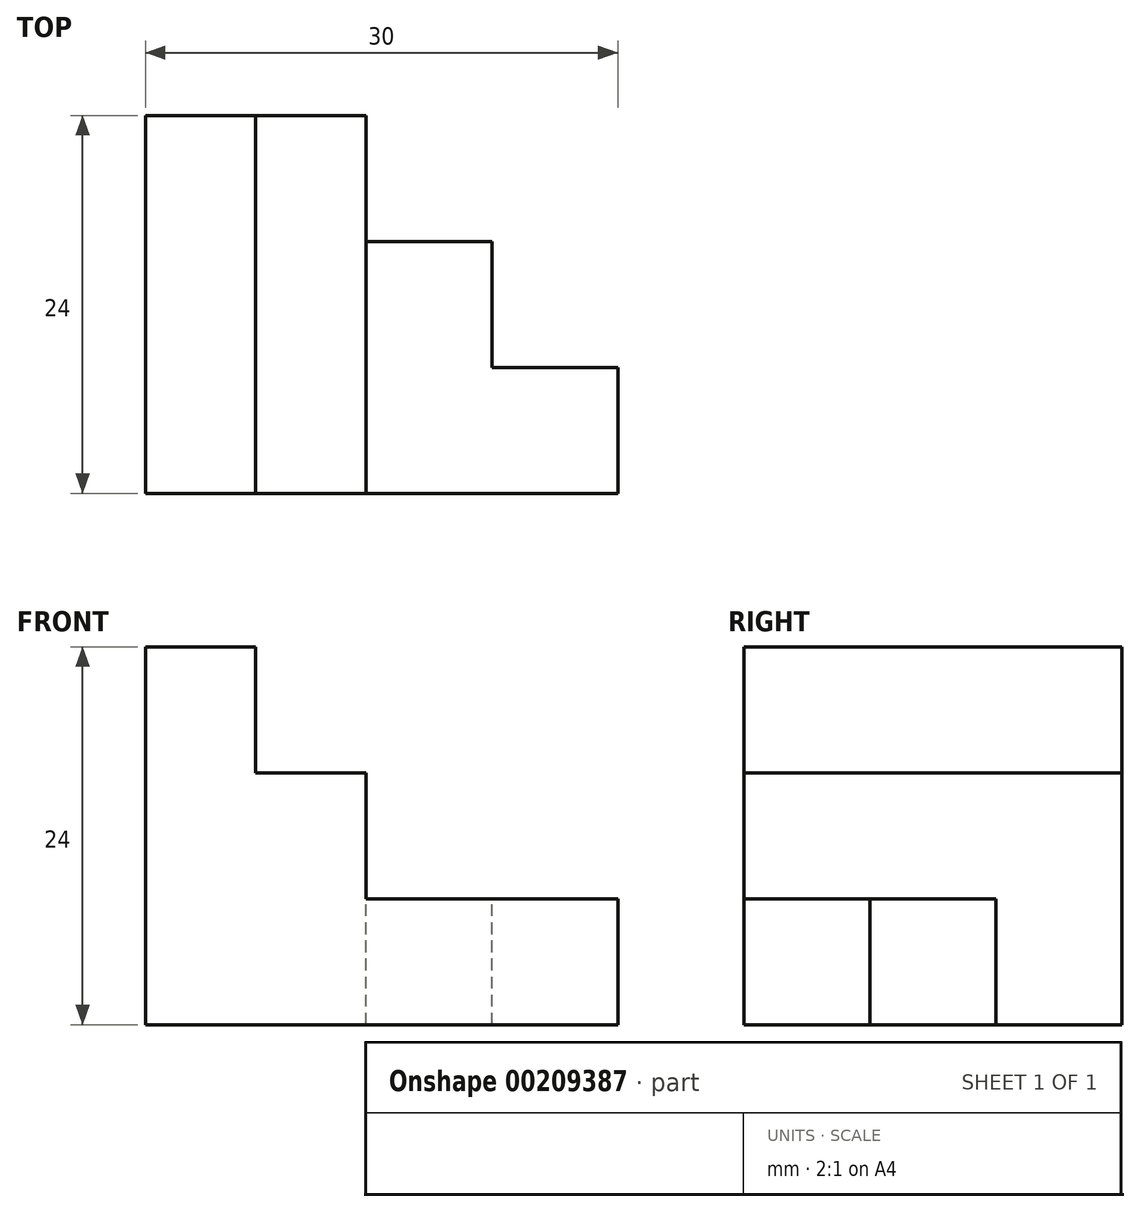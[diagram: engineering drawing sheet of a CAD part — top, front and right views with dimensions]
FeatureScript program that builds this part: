
annotation { "Feature Type Name" : "Feature", "Feature Type Description" : "" }
export const myFeature = defineFeature(function(context is Context, id is Id, definition is map)
    precondition{}
    {
        {
            var Q0;
            Q0=qCreatedBy(makeId("Top.planeOp"),FACE);
            var sketch = newSketch(context, id + "F0", { "sketchPlane" : qUnion([Q0])});
            skLineSegment(sketch, "E0.bottom", {"start": v(0, 0) * mm, "end": v(30, 0) * mm});
            skLineSegment(sketch, "E0.top", {"start": v(0, 24) * mm, "end": v(30, 24) * mm});
            skLineSegment(sketch, "E0.left", {"start": v(0, 0) * mm, "end": v(0, 24) * mm});
            skLineSegment(sketch, "E0.right", {"start": v(30, 0) * mm, "end": v(30, 24) * mm});
            skSolve(sketch);
        }
        {
            var Q0;
            Q0=makeQuery(id+"F0.imprint","IMPRINT",FACE,{"disambiguationData":[TD([[makeQuery(id+"F0.imprint","IMPRINT",EDGE,{"derivedFrom":sQuery(id+"F0.wireOp",EDGE,"E0.bottom")}),1.0]])]});
            extrude(context, id + "F1", {"entities" : qUnion([Q0]), "depth" : 24 * mm});
        }
        {
            var Q0;
            Q0=makeQuery(id+"F1.opExtrude","CAP_FACE",FACE,{"disambiguationData":[OSD([sQuery(id+"F0.wireOp",EDGE,"E0.bottom"),sQuery(id+"F0.wireOp",EDGE,"E0.top"),sQuery(id+"F0.wireOp",EDGE,"E0.left"),sQuery(id+"F0.wireOp",EDGE,"E0.right")])],"isStart":false});
            var sketch = newSketch(context, id + "F2", { "sketchPlane" : qUnion([Q0])});
            skLineSegment(sketch, "E1", {"start": v(30, 0) * mm, "end": v(30, 8) * mm});
            skLineSegment(sketch, "E2", {"start": v(30, 8) * mm, "end": v(22, 8) * mm});
            skLineSegment(sketch, "E3", {"start": v(22, 8) * mm, "end": v(22, 16) * mm});
            skLineSegment(sketch, "E4", {"start": v(22, 16) * mm, "end": v(14, 16) * mm});
            skLineSegment(sketch, "E5", {"start": v(14, 16) * mm, "end": v(14, 0) * mm});
            skPoint(sketch, "E5.endSnap0", {"position": v(15, 0) * mm});
            skLineSegment(sketch, "E6", {"start": v(14, 0) * mm, "end": v(30, 0) * mm});
            skLineSegment(sketch, "E7", {"start": v(14, 16) * mm, "end": v(14, 24) * mm});
            skLineSegment(sketch, "E8", {"start": v(14, 24) * mm, "end": v(30, 24) * mm});
            skLineSegment(sketch, "E9", {"start": v(30, 24) * mm, "end": v(30, 8) * mm});
            skSolve(sketch);
        }
        {
            var Q0;
            Q0=makeQuery(id+"F2.imprint","IMPRINT",FACE,{"disambiguationData":[TD([[makeQuery(id+"F2.imprint","IMPRINT",EDGE,{"derivedFrom":sQuery(id+"F2.wireOp",EDGE,"E1")}),1.0]])]});
            extrude(context, id + "F3", {"entities" : qUnion([Q0]), "operationType" : NewBodyOperationType.REMOVE, "oppositeDirection" : true, "depth" : 16 * mm});
        }
        {
            var Q0;
            Q0=makeQuery(id+"F1.opExtrude","CAP_FACE",FACE,{"disambiguationData":[OSD([sQuery(id+"F0.wireOp",EDGE,"E0.bottom"),sQuery(id+"F0.wireOp",EDGE,"E0.top"),sQuery(id+"F0.wireOp",EDGE,"E0.left"),sQuery(id+"F0.wireOp",EDGE,"E0.right")])],"isStart":false});
            var sketch = newSketch(context, id + "F4", { "sketchPlane" : qUnion([Q0])});
            skLineSegment(sketch, "E10", {"start": v(0, 24) * mm, "end": v(7, 24) * mm});
            skLineSegment(sketch, "E11", {"start": v(7, 24) * mm, "end": v(7, 0) * mm});
            skLineSegment(sketch, "E12", {"start": v(7, 0) * mm, "end": v(0, 0) * mm});
            skLineSegment(sketch, "E13", {"start": v(0, 0) * mm, "end": v(0, 24) * mm});
            skLineSegment(sketch, "E14", {"start": v(14, 16) * mm, "end": v(14, 24) * mm});
            skLineSegment(sketch, "E15", {"start": v(14, 24) * mm, "end": v(30, 24) * mm});
            skLineSegment(sketch, "E16", {"start": v(30, 24) * mm, "end": v(30, 8) * mm});
            skLineSegment(sketch, "E17", {"start": v(30, 8) * mm, "end": v(22, 8) * mm});
            skLineSegment(sketch, "E18", {"start": v(22, 8) * mm, "end": v(22, 16) * mm});
            skLineSegment(sketch, "E19", {"start": v(22, 16) * mm, "end": v(14, 16) * mm});
            skSolve(sketch);
        }
        {
            var Q0;
            {var subQ1=sQuery(id+"F4.wireOp",EDGE,"E11");Q0=makeQuery(id+"F4.imprint","IMPRINT",FACE,{"disambiguationData":[TD([[makeQuery(id+"F4.imprint","IMPRINT",EDGE,{"derivedFrom":subQ1}),1.0]])]});}
            extrude(context, id + "F5", {"entities" : qUnion([Q0]), "operationType" : NewBodyOperationType.REMOVE, "oppositeDirection" : true, "depth" : 8 * mm});
        }
        {
            var Q0;
            {var subQ0=sQuery(id+"F0.wireOp",EDGE,"E0.top");var subQ1=sQuery(id+"F0.wireOp",EDGE,"E0.right");Q0=makeQuery(id+"F5.boolean.opBoolean","SPLIT",FACE,{"disambiguationData":[TD([makeQuery(id+"F1.opExtrude","SWEPT_FACE",FACE,{"disambiguationData":[OSD([subQ1])]})])],"derivedFrom":makeQuery(id+"F1.opExtrude","CAP_FACE",FACE,{"disambiguationData":[OSD([sQuery(id+"F0.wireOp",EDGE,"E0.bottom"),subQ0,sQuery(id+"F0.wireOp",EDGE,"E0.left"),subQ1])],"isStart":false})});}
            extrude(context, id + "F6", {"entities" : qUnion([Q0]), "operationType" : NewBodyOperationType.ADD, "oppositeDirection" : true, "depth" : 16 * mm});
        }
        {
            var Q0;
            {var subQ0=sQuery(id+"F0.wireOp",EDGE,"E0.top");var subQ1=sQuery(id+"F0.wireOp",EDGE,"E0.right");Q0=makeQuery(id+"F5.boolean.opBoolean","SPLIT",FACE,{"disambiguationData":[TD([makeQuery(id+"F1.opExtrude","SWEPT_FACE",FACE,{"disambiguationData":[OSD([subQ1])]})])],"derivedFrom":makeQuery(id+"F1.opExtrude","CAP_FACE",FACE,{"disambiguationData":[OSD([sQuery(id+"F0.wireOp",EDGE,"E0.bottom"),subQ0,sQuery(id+"F0.wireOp",EDGE,"E0.left"),subQ1])],"isStart":false})});}
            var sketch = newSketch(context, id + "F7", { "sketchPlane" : qUnion([Q0])});
            skLineSegment(sketch, "E20", {"start": v(22, 16) * mm, "end": v(22, 24) * mm});
            skLineSegment(sketch, "E21", {"start": v(22, 24) * mm, "end": v(14, 24) * mm});
            skLineSegment(sketch, "E22", {"start": v(14, 24) * mm, "end": v(14, 16) * mm});
            skLineSegment(sketch, "E23", {"start": v(14, 16) * mm, "end": v(22, 16) * mm});
            skSolve(sketch);
        }
        {
            var Q0;
            Q0=makeQuery(id+"F7.imprint","IMPRINT",FACE,{"disambiguationData":[TD([[makeQuery(id+"F7.imprint","IMPRINT",EDGE,{"derivedFrom":sQuery(id+"F7.wireOp",EDGE,"E20")}),1.0]])]});
            extrude(context, id + "F8", {"entities" : qUnion([Q0]), "operationType" : NewBodyOperationType.REMOVE, "oppositeDirection" : true, "depth" : 24 * mm});
        }
        {
            var Q0;
            {var subQ0=sQuery(id+"F0.wireOp",EDGE,"E0.top");var subQ1=sQuery(id+"F0.wireOp",EDGE,"E0.right");Q0=makeQuery(id+"F5.boolean.opBoolean","SPLIT",FACE,{"disambiguationData":[TD([makeQuery(id+"F1.opExtrude","SWEPT_FACE",FACE,{"disambiguationData":[OSD([subQ1])]})])],"derivedFrom":makeQuery(id+"F1.opExtrude","CAP_FACE",FACE,{"disambiguationData":[OSD([sQuery(id+"F0.wireOp",EDGE,"E0.bottom"),subQ0,sQuery(id+"F0.wireOp",EDGE,"E0.left"),subQ1])],"isStart":false})});}
            extrude(context, id + "F9", {"entities" : qUnion([Q0]), "operationType" : NewBodyOperationType.REMOVE, "oppositeDirection" : true, "depth" : 24 * mm});
        }
    });
